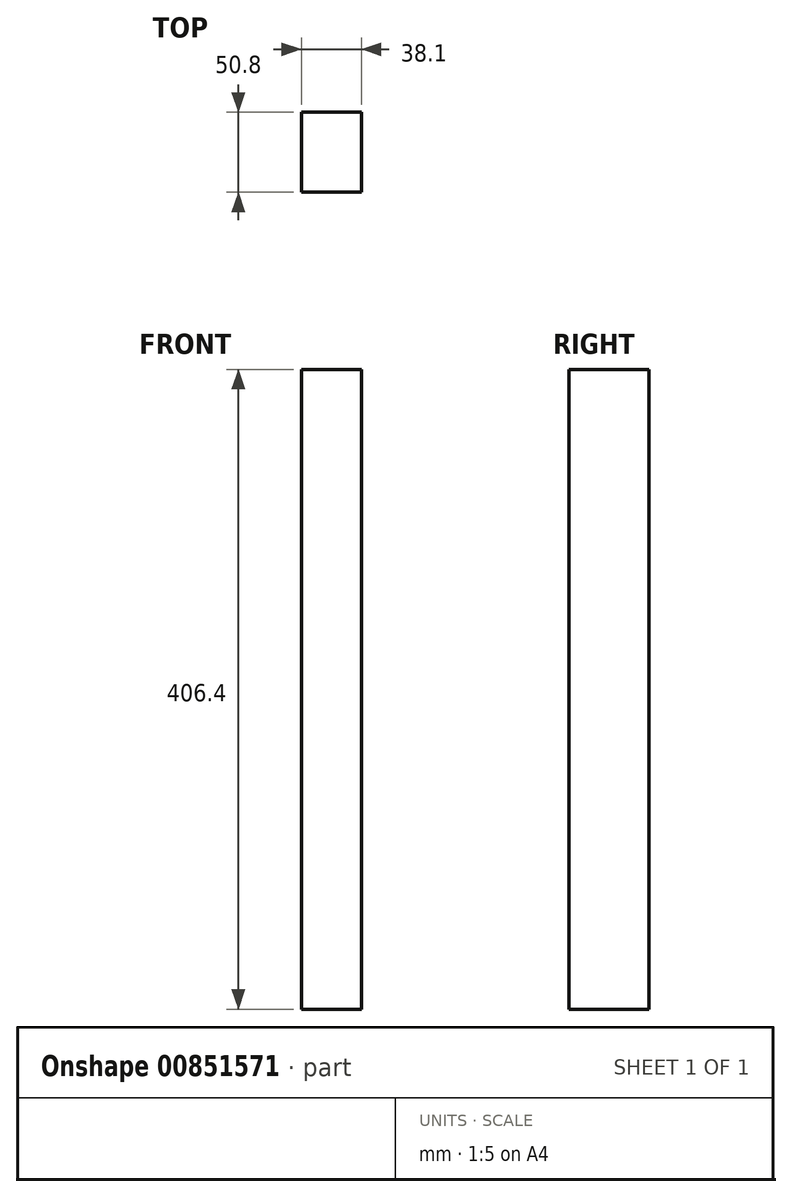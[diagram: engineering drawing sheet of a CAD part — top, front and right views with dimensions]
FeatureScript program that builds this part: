
annotation { "Feature Type Name" : "Feature", "Feature Type Description" : "" }
export const myFeature = defineFeature(function(context is Context, id is Id, definition is map)
    precondition{}
    {
        {
            var Q0;
            Q0=qCreatedBy(makeId("Front.planeOp"),FACE);
            var sketch = newSketch(context, id + "F0", { "sketchPlane" : qUnion([Q0])});
            skLineSegment(sketch, "E0.bottom", {"start": v(-101.17, 212.02) * mm, "end": v(-63.07, 212.02) * mm});
            skLineSegment(sketch, "E0.top", {"start": v(-101.17, -194.38) * mm, "end": v(-63.07, -194.38) * mm});
            skLineSegment(sketch, "E0.left", {"start": v(-101.17, 212.02) * mm, "end": v(-101.17, -194.38) * mm});
            skLineSegment(sketch, "E0.right", {"start": v(-63.07, 212.02) * mm, "end": v(-63.07, -194.38) * mm});
            skSolve(sketch);
        }
        {
            var Q0;
            Q0 = qSketchRegion(id + "F0", true);
            extrude(context, id + "F1", {"entities" : qUnion([Q0]), "depth" : 50.8 * mm, "offsetDistance" : 25.4 * mm});
        }
    });
